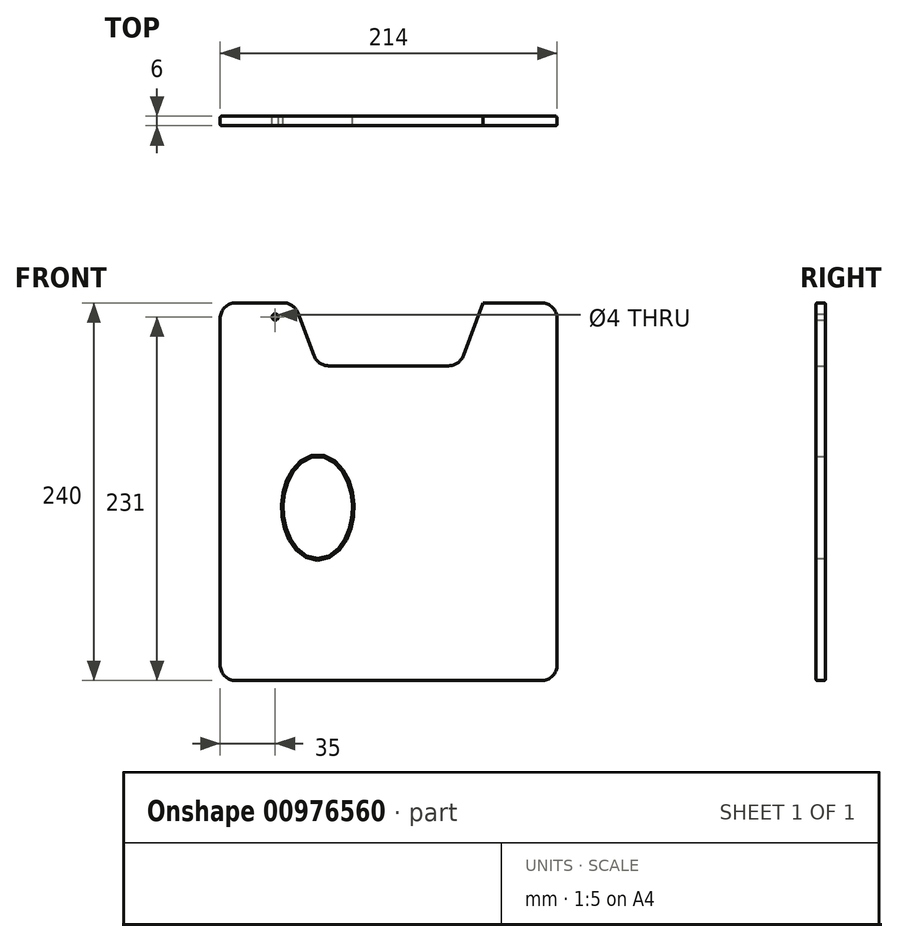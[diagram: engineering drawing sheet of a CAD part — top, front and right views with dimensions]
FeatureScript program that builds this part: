
annotation { "Feature Type Name" : "Feature", "Feature Type Description" : "" }
export const myFeature = defineFeature(function(context is Context, id is Id, definition is map)
    precondition{}
    {
        {
            var Q0;
            Q0=qCreatedBy(makeId("Front.planeOp"),FACE);
            var sketch = newSketch(context, id + "F0", { "sketchPlane" : qUnion([Q0])});
            skLineSegment(sketch, "E0.bottom", {"start": v(-107, 0) * mm, "end": v(107, 0) * mm});
            skLineSegment(sketch, "E0.top", {"start": v(-107, -240) * mm, "end": v(107, -240) * mm});
            skLineSegment(sketch, "E0.left", {"start": v(-107, 0) * mm, "end": v(-107, -240) * mm});
            skLineSegment(sketch, "E0.right", {"start": v(107, 0) * mm, "end": v(107, -240) * mm});
            skSolve(sketch);
        }
        {
            var Q0;
            Q0=makeQuery(id+"F0.imprint","IMPRINT",FACE,{"disambiguationData":[TD([[makeQuery(id+"F0.imprint","IMPRINT",EDGE,{"derivedFrom":sQuery(id+"F0.wireOp",EDGE,"E0.bottom")}),-1.0]])]});
            extrude(context, id + "F1", {"entities" : qUnion([Q0]), "depth" : 6 * mm, "offsetDistance" : 25 * mm});
        }
        {
            var Q0;
            Q0=qCreatedBy(makeId("Front.planeOp"),FACE);
            var sketch = newSketch(context, id + "F2", { "sketchPlane" : qUnion([Q0])});
            skPoint(sketch, "E1", {"position": v(-72, -9) * mm});
            skSolve(sketch);
        }
        {
            var Q0;
            Q0=sQuery(id+"F2.wireOp",VERTEX,"E1");
            var Q1;
            Q1=makeQuery(id+"F1.opExtrude","SWEPT_BODY",BODY,{"disambiguationData":[OSD([sQuery(id+"F0.wireOp",EDGE,"E0.bottom"),sQuery(id+"F0.wireOp",EDGE,"E0.top"),sQuery(id+"F0.wireOp",EDGE,"E0.left"),sQuery(id+"F0.wireOp",EDGE,"E0.right")])]});
            hole(context, id + "F3", {"style" : HoleStyle.SIMPLE, "endStyle" : HoleEndStyle.THROUGH, "oppositeDirection" : true, "holeDiameter" : 4 * mm, "majorDiameter" : 5 * mm, "isTappedThrough" : true, "tappedDepth" : 12 * mm, "tapClearance" : 3, "startFromSketch" : true, "locations" : qUnion([Q0]), "scope" : qUnion([Q1])});
        }
        {
            var Q0;
            Q0=qCreatedBy(makeId("Front.planeOp"),FACE);
            var sketch = newSketch(context, id + "F4", { "sketchPlane" : qUnion([Q0])});
            skEllipse(sketch, "E2", {"center": v(-45, -130) * mm, "majorRadius": 32.5 * mm, "minorRadius": 22 * mm, "majorAxis": v(0, -1)});
            skSolve(sketch);
        }
        {
            var Q0;
            Q0=makeQuery(id+"F4.imprint","IMPRINT",FACE,{"disambiguationData":[TD([[makeQuery(id+"F4.imprint","IMPRINT",EDGE,{"derivedFrom":sQuery(id+"F4.wireOp",EDGE,"E2")}),1.0]])]});
            extrude(context, id + "F5", {"entities" : qUnion([Q0]), "operationType" : NewBodyOperationType.REMOVE, "endBound" : BoundingType.THROUGH_ALL, "depth" : 25 * mm, "offsetDistance" : 25 * mm});
        }
        {
            var Q0;
            Q0=qCreatedBy(makeId("Front.planeOp"),FACE);
            var sketch = newSketch(context, id + "F6", { "sketchPlane" : qUnion([Q0])});
            skLineSegment(sketch, "E3.bottom", {"start": v(-60, 0) * mm, "end": v(60, 0) * mm});
            skLineSegment(sketch, "E3.left", {"start": v(-60, 0) * mm, "end": v(-45, -40) * mm});
            skLineSegment(sketch, "E3.right", {"start": v(60, 0) * mm, "end": v(45, -40) * mm});
            skLineSegment(sketch, "E4", {"start": v(0, -112) * mm, "end": v(0, 0) * mm, "construction": true});
            skPoint(sketch, "E4.startSnap0", {"position": v(0, -40) * mm});
            skLineSegment(sketch, "E5", {"start": v(45, -40) * mm, "end": v(-45, -40) * mm});
            skSolve(sketch);
        }
        {
            var Q0;
            Q0=makeQuery(id+"F6.imprint","IMPRINT",FACE,{"disambiguationData":[TD([[makeQuery(id+"F6.imprint","IMPRINT",EDGE,{"derivedFrom":sQuery(id+"F6.wireOp",EDGE,"E3.bottom")}),-1.0]])]});
            extrude(context, id + "F7", {"entities" : qUnion([Q0]), "operationType" : NewBodyOperationType.REMOVE, "endBound" : BoundingType.THROUGH_ALL, "depth" : 25 * mm, "offsetDistance" : 25 * mm});
        }
        {
            var Q0;
            Q0=makeQuery(id+"F1.opExtrude","SWEPT_EDGE",EDGE,{"disambiguationData":[OSD([sQuery(id+"F0.wireOp",EDGE,"E0.top"),sQuery(id+"F0.wireOp",EDGE,"E0.left")])]});
            var Q1;
            Q1=makeQuery(id+"F1.opExtrude","SWEPT_EDGE",EDGE,{"disambiguationData":[OSD([sQuery(id+"F0.wireOp",EDGE,"E0.bottom"),sQuery(id+"F0.wireOp",EDGE,"E0.left")])]});
            var Q2;
            Q2=makeQuery(id+"F1.opExtrude","SWEPT_EDGE",EDGE,{"disambiguationData":[OSD([sQuery(id+"F0.wireOp",EDGE,"E0.bottom"),sQuery(id+"F0.wireOp",EDGE,"E0.right")])]});
            var Q3;
            Q3=makeQuery(id+"F1.opExtrude","SWEPT_EDGE",EDGE,{"disambiguationData":[OSD([sQuery(id+"F0.wireOp",EDGE,"E0.top"),sQuery(id+"F0.wireOp",EDGE,"E0.right")])]});
            var Q4;
            Q4=makeQuery(id+"F0KkT8lZ60NvEae_1.opExtrude","SWEPT_EDGE",EDGE,{"disambiguationData":[OSD([sQuery(id+"FPDMrndPVMWiteg_1.wireOp",EDGE,"VOKADtWJ-iiXs-hyUV-8ADC-n0sSMjc71uTK"),sQuery(id+"FPDMrndPVMWiteg_1.wireOp",EDGE,"VAbbkKxT-lXHb-kVAA-uLZe-Vs4TNUvW595M")])]});
            var Q5;
            Q5=makeQuery(id+"F7.boolean.opBoolean","COPY",EDGE,{"derivedFrom":makeQuery(id+"F7.opExtrude","SWEPT_EDGE",EDGE,{"disambiguationData":[OSD([sQuery(id+"F6.wireOp",EDGE,"E3.bottom"),sQuery(id+"F6.wireOp",EDGE,"E3.left")])]})});
            var Q6;
            Q6=makeQuery(id+"F7.boolean.opBoolean","COPY",EDGE,{"derivedFrom":makeQuery(id+"F7.opExtrude","SWEPT_EDGE",EDGE,{"disambiguationData":[OSD([sQuery(id+"F6.wireOp",EDGE,"E3.left"),sQuery(id+"F6.wireOp",EDGE,"E5")])]})});
            var Q7;
            Q7=makeQuery(id+"F7.boolean.opBoolean","COPY",EDGE,{"derivedFrom":makeQuery(id+"F7.opExtrude","SWEPT_EDGE",EDGE,{"disambiguationData":[OSD([sQuery(id+"F6.wireOp",EDGE,"E3.bottom"),sQuery(id+"F6.wireOp",EDGE,"E3.right")])]})});
            var Q8;
            Q8=makeQuery(id+"F7.boolean.opBoolean","COPY",EDGE,{"derivedFrom":makeQuery(id+"F7.opExtrude","SWEPT_EDGE",EDGE,{"disambiguationData":[OSD([sQuery(id+"F6.wireOp",EDGE,"E3.right"),sQuery(id+"F6.wireOp",EDGE,"E5")])]})});
            var Q9;
            Q9=makeQuery(id+"F0KkT8lZ60NvEae_1.opExtrude","SWEPT_EDGE",EDGE,{"disambiguationData":[OSD([sQuery(id+"FPDMrndPVMWiteg_1.wireOp",EDGE,"VAbbkKxT-lXHb-kVAA-uLZe-Vs4TNUvW595M"),sQuery(id+"FPDMrndPVMWiteg_1.wireOp",EDGE,"NMe8SefL-qBYR-ohaw-Zb7G-82egpqT0p6MS")])]});
            var Q10;
            Q10=makeQuery(id+"FMalZsQbwLfM2XQ_1.1.F0KkT8lZ60NvEae_1.opExtrude","SWEPT_EDGE",EDGE,{"disambiguationData":[OSD([sQuery(id+"FPDMrndPVMWiteg_1.wireOp",EDGE,"VAbbkKxT-lXHb-kVAA-uLZe-Vs4TNUvW595M"),sQuery(id+"FPDMrndPVMWiteg_1.wireOp",EDGE,"NMe8SefL-qBYR-ohaw-Zb7G-82egpqT0p6MS")])]});
            var Q11;
            Q11=makeQuery(id+"FMalZsQbwLfM2XQ_1.1.F0KkT8lZ60NvEae_1.opExtrude","SWEPT_EDGE",EDGE,{"disambiguationData":[OSD([sQuery(id+"FPDMrndPVMWiteg_1.wireOp",EDGE,"VOKADtWJ-iiXs-hyUV-8ADC-n0sSMjc71uTK"),sQuery(id+"FPDMrndPVMWiteg_1.wireOp",EDGE,"VAbbkKxT-lXHb-kVAA-uLZe-Vs4TNUvW595M")])]});
            var Q12;
            Q12=makeQuery(id+"FMalZsQbwLfM2XQ_1.1.F0KkT8lZ60NvEae_1.opExtrude","SWEPT_EDGE",EDGE,{"disambiguationData":[OSD([sQuery(id+"FPDMrndPVMWiteg_1.wireOp",EDGE,"51GGUbov-XiVD-KQ26-Cb1m-a7Oa3ILeiFkA"),sQuery(id+"FPDMrndPVMWiteg_1.wireOp",EDGE,"VOKADtWJ-iiXs-hyUV-8ADC-n0sSMjc71uTK")])]});
            var Q13;
            Q13=makeQuery(id+"F0KkT8lZ60NvEae_1.opExtrude","SWEPT_EDGE",EDGE,{"disambiguationData":[OSD([sQuery(id+"FPDMrndPVMWiteg_1.wireOp",EDGE,"51GGUbov-XiVD-KQ26-Cb1m-a7Oa3ILeiFkA"),sQuery(id+"FPDMrndPVMWiteg_1.wireOp",EDGE,"VOKADtWJ-iiXs-hyUV-8ADC-n0sSMjc71uTK")])]});
            fillet(context, id + "F8", {"entities" : qUnion([Q0, Q1, Q2, Q3, Q4, Q5, Q6, Q7, Q8, Q9, Q10, Q11, Q12, Q13]), "radius" : 10 * mm, "tangentPropagation" : true, "defaultsChanged" : true, "vertexSettings" : [], "allowEdgeOverflow" : false});
        }
        {
            var Q0;
            Q0=makeQuery(id+"F1.opExtrude","CAP_EDGE",EDGE,{"disambiguationData":[OSD([sQuery(id+"F0.wireOp",EDGE,"E0.right")])],"isStart":true});
            var Q1;
            Q1=makeQuery(id+"F1.opExtrude","CAP_EDGE",EDGE,{"disambiguationData":[OSD([sQuery(id+"F0.wireOp",EDGE,"E0.right")])],"isStart":false});
            var Q2;
            Q2=makeQuery(id+"F5.boolean.opBoolean","INTERSECT",EDGE,{"derivedFrom":[makeQuery(id+"F1.opExtrude","CAP_FACE",FACE,{"disambiguationData":[OSD([sQuery(id+"F0.wireOp",EDGE,"E0.bottom"),sQuery(id+"F0.wireOp",EDGE,"E0.top"),sQuery(id+"F0.wireOp",EDGE,"E0.left"),sQuery(id+"F0.wireOp",EDGE,"E0.right")])],"isStart":false}),makeQuery(id+"F5.opExtrude","SWEPT_FACE",FACE,{"disambiguationData":[OSD([sQuery(id+"F4.wireOp",EDGE,"E2")])]})]});
            var Q3;
            Q3=makeQuery(id+"FMalZsQbwLfM2XQ_1.1.F5.boolean.opBoolean","INTERSECT",EDGE,{"derivedFrom":[makeQuery(id+"F1.opExtrude","CAP_FACE",FACE,{"disambiguationData":[OSD([sQuery(id+"F0.wireOp",EDGE,"E0.bottom"),sQuery(id+"F0.wireOp",EDGE,"E0.top"),sQuery(id+"F0.wireOp",EDGE,"E0.left"),sQuery(id+"F0.wireOp",EDGE,"E0.right")])],"isStart":false}),makeQuery(id+"FMalZsQbwLfM2XQ_1.1.F5.opExtrude","SWEPT_FACE",FACE,{"disambiguationData":[OSD([sQuery(id+"F4.wireOp",EDGE,"E2")])]})]});
            var Q4;
            Q4=makeQuery(id+"F5.boolean.opBoolean","COPY",EDGE,{"derivedFrom":makeQuery(id+"F5.opExtrude","CAP_EDGE",EDGE,{"disambiguationData":[OSD([sQuery(id+"F4.wireOp",EDGE,"E2")])],"isStart":true})});
            var Q5;
            Q5=makeQuery(id+"FMalZsQbwLfM2XQ_1.1.F5.boolean.opBoolean","COPY",EDGE,{"derivedFrom":makeQuery(id+"FMalZsQbwLfM2XQ_1.1.F5.opExtrude","CAP_EDGE",EDGE,{"disambiguationData":[OSD([sQuery(id+"F4.wireOp",EDGE,"E2")])],"isStart":true})});
            var Q6;
            {var subQ0=sQuery(id+"F0.wireOp",EDGE,"E0.left");var subQ1=sQuery(id+"F0.wireOp",EDGE,"E0.top");Q6=makeQuery(id+"FVj3dx7qo14AICR_1.boolean.opBoolean","SPLIT",EDGE,{"disambiguationData":[TD([makeQuery(id+"F1.opExtrude","SWEPT_FACE",FACE,{"disambiguationData":[OSD([subQ0])]})])],"derivedFrom":makeQuery(id+"F1.opExtrude","CAP_EDGE",EDGE,{"disambiguationData":[OSD([subQ1])],"isStart":false})});}
            var Q7;
            Q7=makeQuery(id+"FVj3dx7qo14AICR_1.opExtrude","CAP_EDGE",EDGE,{"disambiguationData":[OSD([sQuery(id+"FbXTp0vLZPVL5cG_1.wireOp",EDGE,"kh4IhWl8-fNuQ-XkF3-d1sT-45t9IGdodjkP")])],"isStart":false});
            var Q8;
            Q8=makeQuery(id+"FVj3dx7qo14AICR_1.opExtrude","CAP_EDGE",EDGE,{"disambiguationData":[OSD([sQuery(id+"FbXTp0vLZPVL5cG_1.wireOp",EDGE,"kh4IhWl8-fNuQ-XkF3-d1sT-45t9IGdodjkP")])],"isStart":true});
            var Q9;
            {var subQ0=sQuery(id+"F0.wireOp",EDGE,"E0.left");var subQ1=sQuery(id+"F0.wireOp",EDGE,"E0.top");Q9=makeQuery(id+"FVj3dx7qo14AICR_1.boolean.opBoolean","SPLIT",EDGE,{"disambiguationData":[TD([makeQuery(id+"F1.opExtrude","SWEPT_FACE",FACE,{"disambiguationData":[OSD([subQ0])]})])],"derivedFrom":makeQuery(id+"F1.opExtrude","CAP_EDGE",EDGE,{"disambiguationData":[OSD([subQ1])],"isStart":true})});}
            var Q10;
            {var subQ0=sQuery(id+"F0.wireOp",EDGE,"E0.right");var subQ1=sQuery(id+"F0.wireOp",EDGE,"E0.top");Q10=makeQuery(id+"FVj3dx7qo14AICR_1.boolean.opBoolean","SPLIT",EDGE,{"disambiguationData":[TD([makeQuery(id+"F1.opExtrude","SWEPT_FACE",FACE,{"disambiguationData":[OSD([subQ0])]})])],"derivedFrom":makeQuery(id+"F1.opExtrude","CAP_EDGE",EDGE,{"disambiguationData":[OSD([subQ1])],"isStart":true})});}
            fillet(context, id + "F9", {"entities" : qUnion([Q0, Q1, Q2, Q3, Q4, Q5, Q6, Q7, Q8, Q9, Q10]), "radius" : 1 * mm, "tangentPropagation" : true, "defaultsChanged" : false, "vertexSettings" : [], "allowEdgeOverflow" : false});
        }
    });
